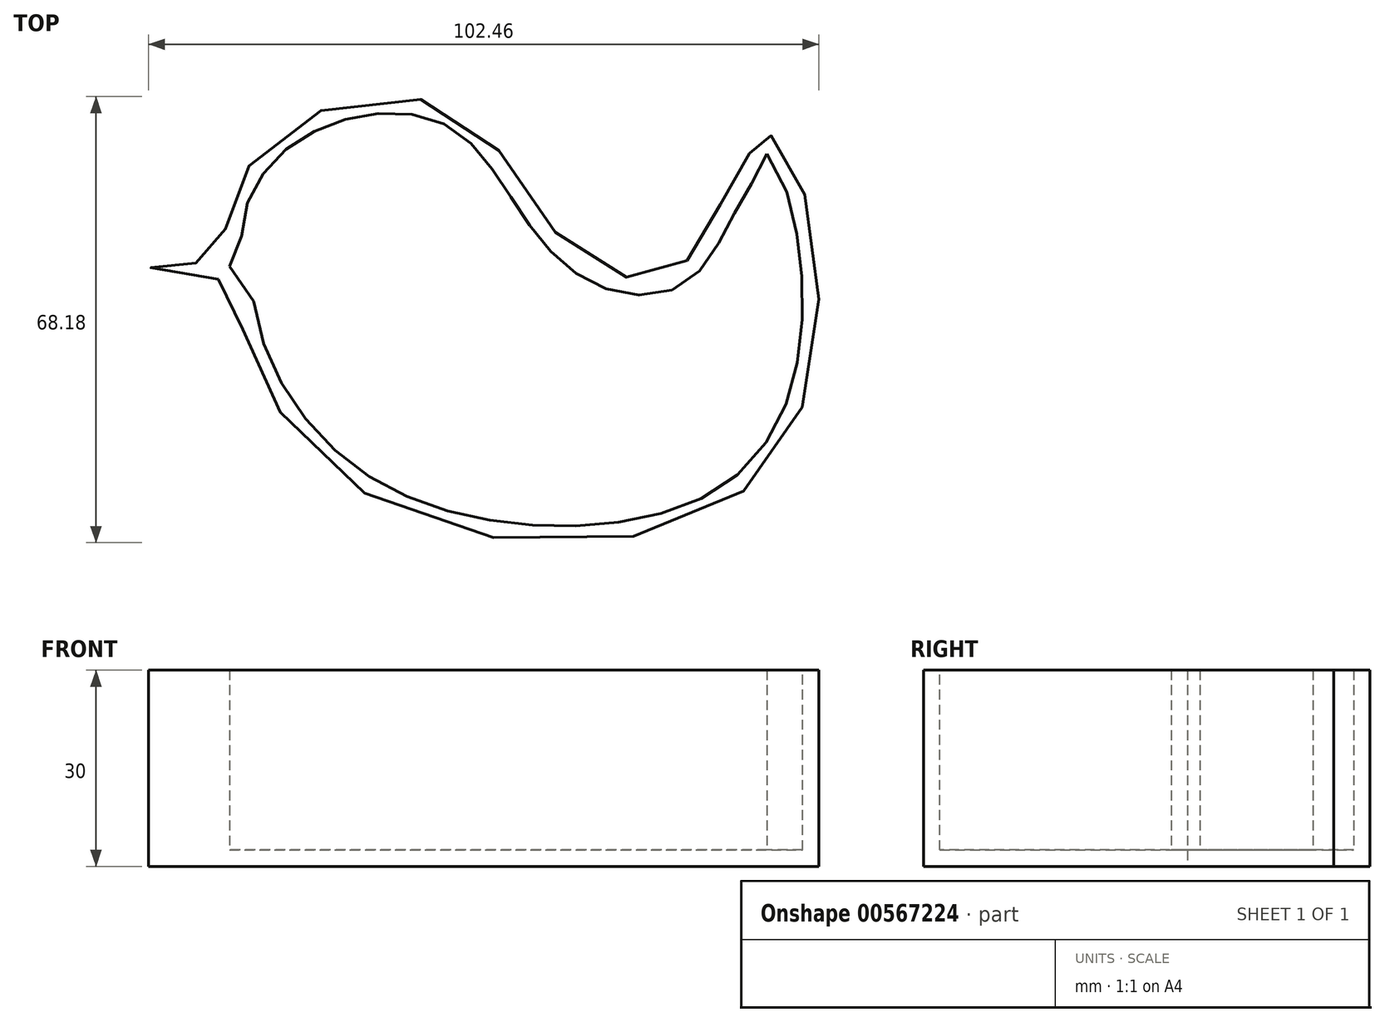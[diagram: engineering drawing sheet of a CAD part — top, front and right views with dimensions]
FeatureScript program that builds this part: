
annotation { "Feature Type Name" : "Feature", "Feature Type Description" : "" }
export const myFeature = defineFeature(function(context is Context, id is Id, definition is map)
    precondition{}
    {
        {
            var Q0;
            Q0=qCreatedBy(makeId("Top.planeOp"),FACE);
            var sketch = newSketch(context, id + "F0", { "sketchPlane" : qUnion([Q0])});
            skFitSpline(sketch, "E0", {"points": [v(44.61, 39.57) * mm, v(39.46, 30.4) * mm, v(32.47, 21.2) * mm, v(17.5, 24.8) * mm, v(0, 45.8) * mm, v(-26.25, 43.26) * mm, v(-35.36, 29.17) * mm, v(-37.17, 23.67) * mm, v(-47.24, 22.1) * mm, v(-36.54, 20.31) * mm, v(-32.54, 11.47) * mm, v(-12.28, -13.49) * mm, v(38.42, -15.42) * mm, v(54.8, 10) * mm, v(50.72, 38.99) * mm, v(46.43, 42.64) * mm, v(44.61, 39.57) * mm]});
            skSolve(sketch);
        }
        {
            var Q0;
            Q0=makeQuery(id+"F0.imprint","IMPRINT",FACE,{"disambiguationData":[TD([[makeQuery(id+"F0.imprint","IMPRINT",EDGE,{"derivedFrom":sQuery(id+"F0.wireOp",EDGE,"E0")}),1.0]])]});
            extrude(context, id + "F1", {"entities" : qUnion([Q0]), "depth" : 30 * mm, "offsetDistance" : 25 * mm});
        }
        {
            var Q0;
            Q0=makeQuery(id+"F1.opExtrude","CAP_FACE",FACE,{"disambiguationData":[OSD([sQuery(id+"F0.wireOp",EDGE,"E0")])],"isStart":false});
            shell(context, id + "F2", {"entities" : qUnion([Q0]), "thickness" : 2.5 * mm});
        }
    });
